# Revit family: POR_MultiSuite_D5862_BIM_NL
name_source: partatom
category: Plumbing Fixtures
revit_build: Autodesk Revit MEP 2016 (Build: 20161004_0715(x64)
units: mm (PartAtom-declared; Revit-internal decimal feet)

## family parameters
Cut with Voids When Loaded = No
Host = Face
OmniClass Number = 23.45.55.21
OmniClass Title = Drains (Wastes)
Part Type = Normal
Room Calculation Point = No
Round Connector Dimension = Use Diameter
Shared = Yes

## types (1)
- D5862AC - BEKERSIPHON   WIT
    Accessories = www.idealstandardnederland.nl
    AreaUnits = millimeters
    Assembly Code = C1030200
    AssetType = Fixed
    BREEAMApproved = No
    BarCode = 3391500312241
    Brand = Porcher
    CWFU = 0
    Color = Wit
    ConnectionType = Sanitair
    Cost = 0 $
    Default Elevation = 800 mm  [stored 2.62467 ft]
    Description = Bekersifon wit
    DurationUnit = year
    ECA = No
    ExpectedLife = 25
    Features = Bekersifon wit
    Finish = Chrome
    FlowRate = ?L/hr @ ?bar
    HWFU = 0
    IfcExportType = sifon
    InstallationInstructions = http://www.idealstandardnederland.nl
    LinearUnits = millimeters
    ManufacturerURL = www.idealstandardnederland.nl
    Material = Kunststof
    Model = D5862AC
    ModelNumber = D5862AC
    ModelReference = Bekersifon wit
    NBSReference = 45-35-70/???
    Name = BEKERSIPHON   WIT
    NettWeight = 0,05 KG
    NominalHeight = 156 mm
    NominalLength = 82 mm
    NominalWidth = 64 mm
    ProductInformation = http://www.idealstandardnederland.nl
    Shape = Gesculptuurd
    Size = 156 x 82 x 64 mm
    Space = Internal
    SpareParts = www.idealstandardnederland.nl
    TMV3 = Yes
    TestPressure = 10 Bar
    URL = www.idealstandardnederland.nl
    Version = 2
    VolumeUnits = liter
    WFU = 0
    WRAS = Yes
    WarrantyDescription = Fabrieksgarantie
    WarrantyDurationParts = 1
    WarrantyDurationUnit = jaar
    WaterEfficientProduct = No
    WorkingPressure = ? Bar

note: [stored X ft] marks values corroborated as IEEE doubles in the binary element streams (Revit-internal decimal feet)

## geometry (parser evidence)
native form markers: Sweep x3
no freeform markers — native parametric forms only
